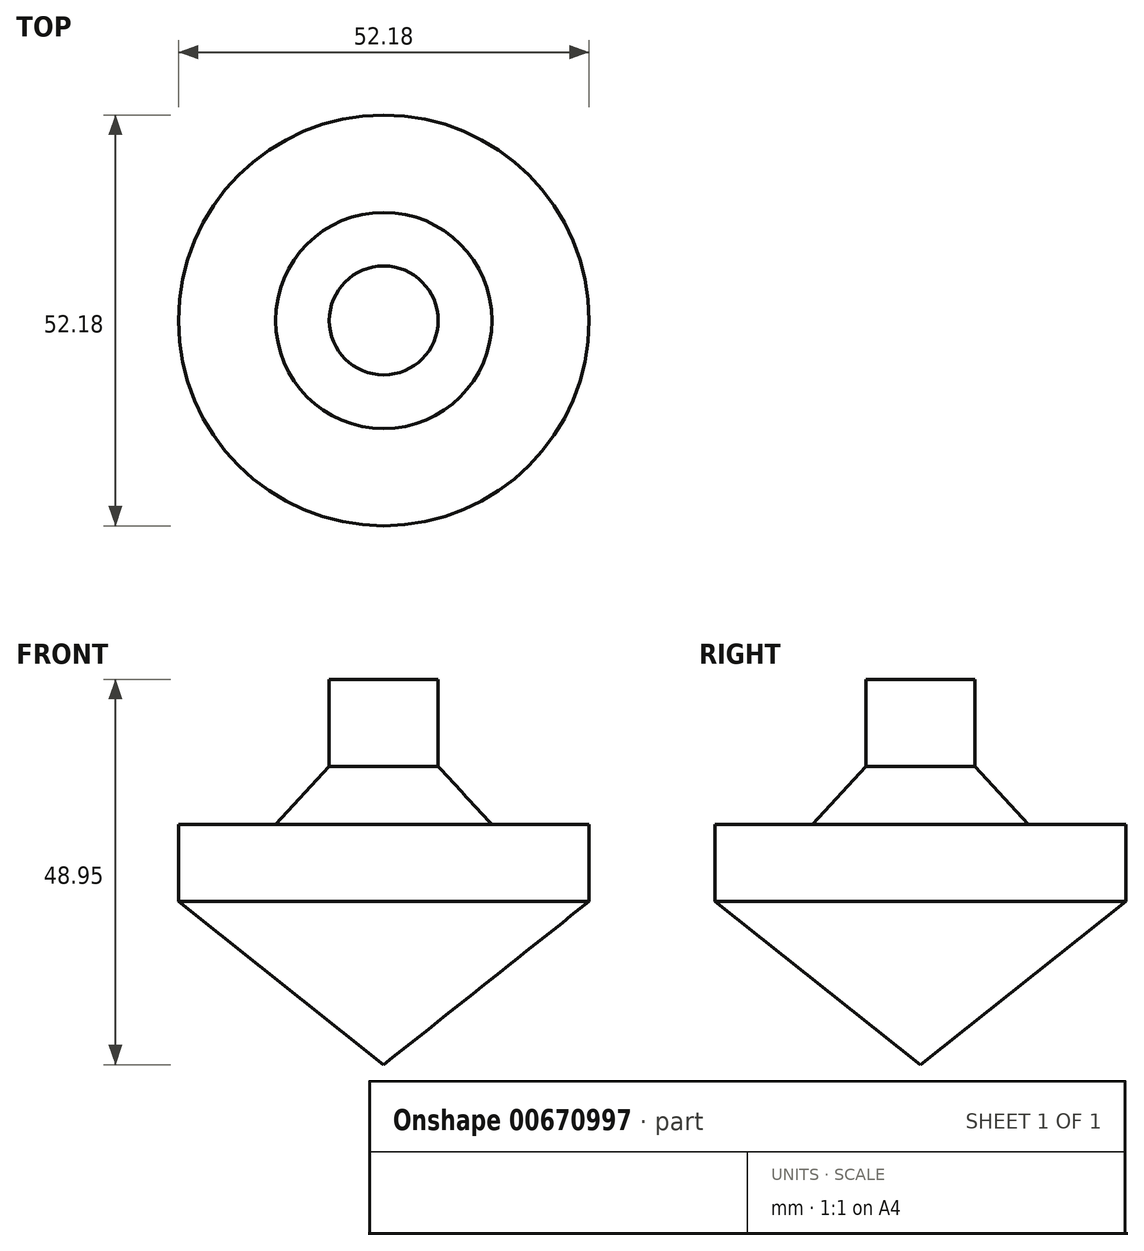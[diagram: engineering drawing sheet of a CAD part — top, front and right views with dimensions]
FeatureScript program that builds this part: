
annotation { "Feature Type Name" : "Feature", "Feature Type Description" : "" }
export const myFeature = defineFeature(function(context is Context, id is Id, definition is map)
    precondition{}
    {
        {
            var Q0;
            Q0=qCreatedBy(makeId("Front.planeOp"),FACE);
            var sketch = newSketch(context, id + "F0", { "sketchPlane" : qUnion([Q0])});
            skLineSegment(sketch, "E0", {"start": v(0, 0) * mm, "end": v(26.09, 20.74) * mm});
            skLineSegment(sketch, "E1", {"start": v(26.09, 20.74) * mm, "end": v(26.09, 30.51) * mm});
            skLineSegment(sketch, "E2", {"start": v(26.09, 30.51) * mm, "end": v(13.73, 30.51) * mm});
            skLineSegment(sketch, "E3", {"start": v(13.73, 30.51) * mm, "end": v(6.91, 37.88) * mm});
            skLineSegment(sketch, "E4", {"start": v(6.91, 37.88) * mm, "end": v(6.91, 48.95) * mm});
            skLineSegment(sketch, "E5", {"start": v(6.91, 48.95) * mm, "end": v(0, 48.95) * mm});
            skLineSegment(sketch, "E6", {"start": v(0, 48.95) * mm, "end": v(0, 0) * mm});
            skSolve(sketch);
        }
        {
            var Q0;
            Q0=qSketchRegion(id+"F0",true);
            var Q1;
            Q1=sQuery(id+"F0.wireOp",EDGE,"E6");
            revolve(context, id + "F1", {"entities" : qUnion([Q0]), "axis" : qUnion([Q1]), "revolveType" : RevolveType.FULL});
        }
    });
